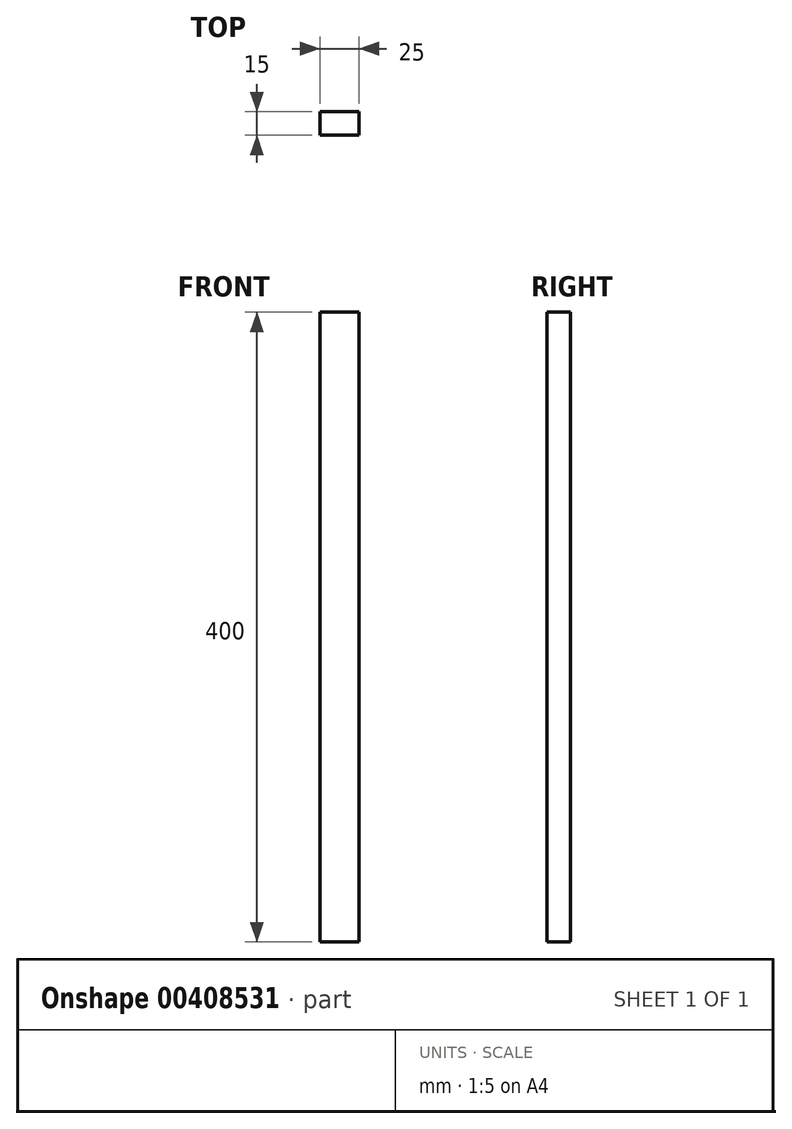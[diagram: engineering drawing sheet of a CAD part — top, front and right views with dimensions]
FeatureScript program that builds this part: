
annotation { "Feature Type Name" : "Feature", "Feature Type Description" : "" }
export const myFeature = defineFeature(function(context is Context, id is Id, definition is map)
    precondition{}
    {
        {
            var Q0;
            Q0=qCreatedBy(makeId("Top.planeOp"),FACE);
            var sketch = newSketch(context, id + "F0", { "sketchPlane" : qUnion([Q0])});
            skLineSegment(sketch, "E0.bottom", {"start": v(12.5, 7.5) * mm, "end": v(-12.5, 7.5) * mm});
            skLineSegment(sketch, "E0.top", {"start": v(12.5, -7.5) * mm, "end": v(-12.5, -7.5) * mm});
            skLineSegment(sketch, "E0.left", {"start": v(12.5, 7.5) * mm, "end": v(12.5, -7.5) * mm});
            skLineSegment(sketch, "E0.right", {"start": v(-12.5, 7.5) * mm, "end": v(-12.5, -7.5) * mm});
            skPoint(sketch, "E0.middle", {"position": v(0, 0) * mm});
            skSolve(sketch);
        }
        {
            var Q0;
            Q0 = qSketchRegion(id + "F0", true);
            extrude(context, id + "F1", {"entities" : qUnion([Q0]), "depth" : 400 * mm});
        }
    });
